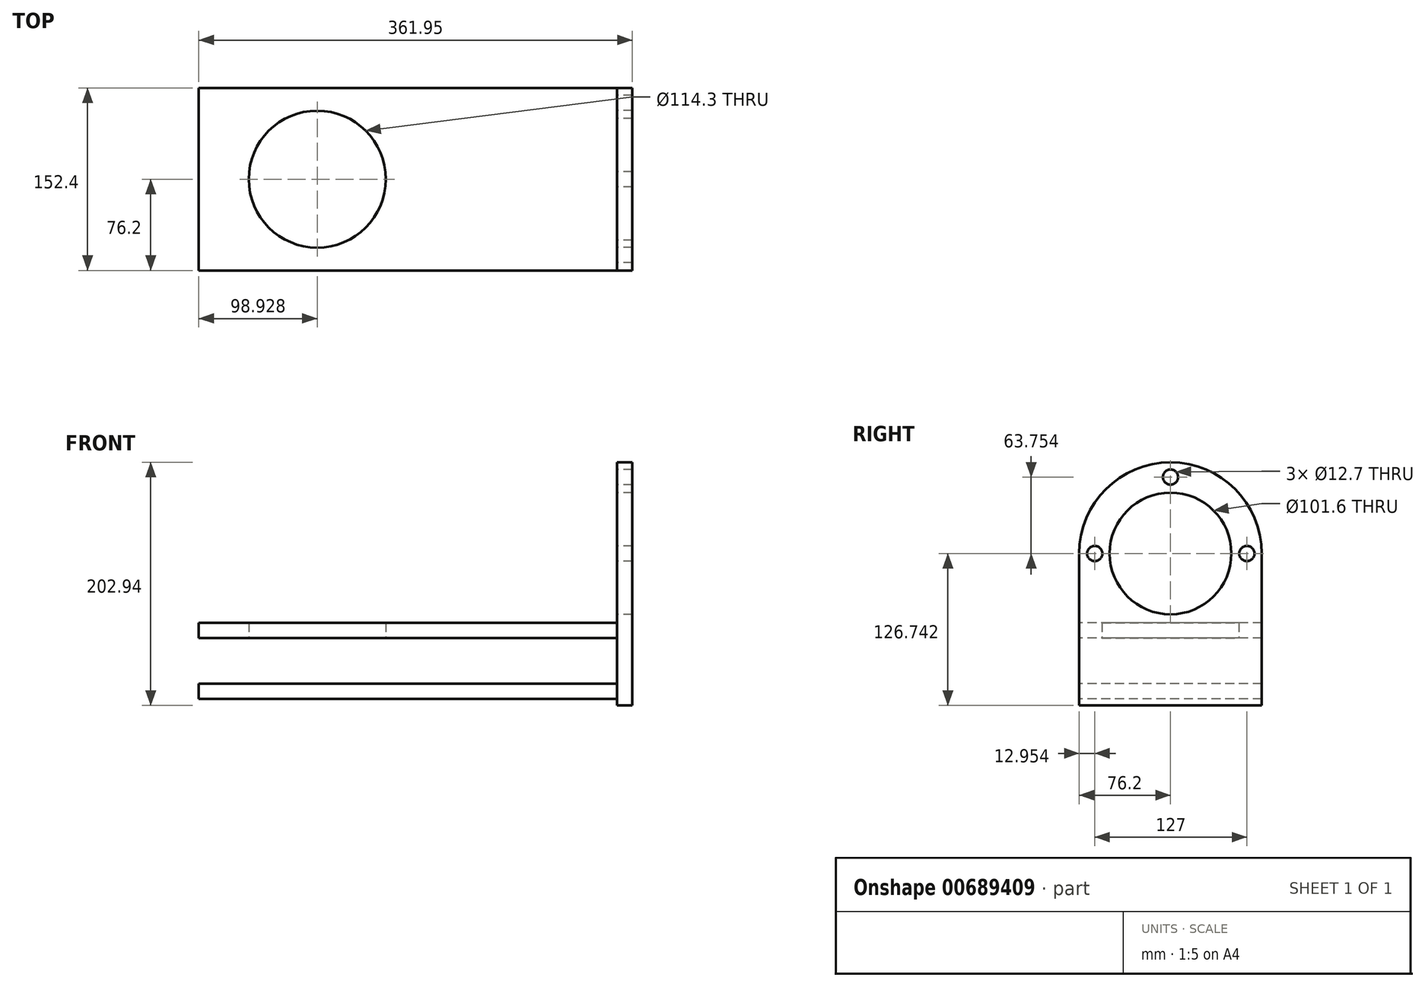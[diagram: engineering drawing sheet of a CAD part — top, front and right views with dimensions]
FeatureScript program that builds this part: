
annotation { "Feature Type Name" : "Feature", "Feature Type Description" : "" }
export const myFeature = defineFeature(function(context is Context, id is Id, definition is map)
    precondition{}
    {
        {
            var Q0;
            Q0=qCreatedBy(makeId("Top.planeOp"),FACE);
            var sketch = newSketch(context, id + "F0", { "sketchPlane" : qUnion([Q0])});
            skLineSegment(sketch, "E0.bottom", {"start": v(-174.63, 76.2) * mm, "end": v(174.63, 76.2) * mm});
            skLineSegment(sketch, "E0.top", {"start": v(-174.63, -76.2) * mm, "end": v(174.63, -76.2) * mm});
            skLineSegment(sketch, "E0.left", {"start": v(-174.62, 76.2) * mm, "end": v(-174.63, -76.2) * mm});
            skLineSegment(sketch, "E0.right", {"start": v(174.63, 76.2) * mm, "end": v(174.63, -76.2) * mm});
            skPoint(sketch, "E0.middle", {"position": v(0, 0) * mm});
            skCircle(sketch, "E1", {"center": v(-75.7, 0) * mm, "radius": 57.15 * mm});
            skSolve(sketch);
        }
        {
            var Q0;
            Q0=makeQuery(id+"F0.imprint","IMPRINT",FACE,{"disambiguationData":[TD([[makeQuery(id+"F0.imprint","IMPRINT",EDGE,{"derivedFrom":sQuery(id+"F0.wireOp",EDGE,"E0.bottom")}),-1.0]])]});
            extrude(context, id + "F1", {"entities" : qUnion([Q0]), "depth" : 12.7 * mm, "offsetDistance" : 25.4 * mm});
        }
        {
            var Q0;
            Q0=makeQuery(id+"F1.opExtrude","CAP_FACE",FACE,{"disambiguationData":[OSD([sQuery(id+"F0.wireOp",EDGE,"E0.bottom"),sQuery(id+"F0.wireOp",EDGE,"E0.top"),sQuery(id+"F0.wireOp",EDGE,"E0.left"),sQuery(id+"F0.wireOp",EDGE,"E0.right"),sQuery(id+"F0.wireOp",EDGE,"E1")])],"isStart":false});
            var sketch = newSketch(context, id + "F2", { "sketchPlane" : qUnion([Q0])});
            skLineSegment(sketch, "E2.bottom", {"start": v(-174.63, 76.2) * mm, "end": v(174.63, 76.2) * mm});
            skLineSegment(sketch, "E2.top", {"start": v(-174.63, -76.2) * mm, "end": v(174.62, -76.2) * mm});
            skLineSegment(sketch, "E2.left", {"start": v(-174.63, 76.2) * mm, "end": v(-174.63, -76.2) * mm});
            skLineSegment(sketch, "E2.right", {"start": v(174.63, 76.2) * mm, "end": v(174.62, -76.2) * mm});
            skPoint(sketch, "E2.middle", {"position": v(0, 0) * mm});
            skSolve(sketch);
        }
        {
            var Q0;
            Q0=makeQuery(id+"F2.imprint","IMPRINT",FACE,{"disambiguationData":[TD([[makeQuery(id+"F2.imprint","IMPRINT",EDGE,{"derivedFrom":sQuery(id+"F2.wireOp",EDGE,"E2.bottom")}),-1.0]])]});
            var Q1;
            Q1=makeQuery(id+"F2.imprint","IMPRINT",FACE,{"disambiguationData":[TD([[makeQuery(id+"F2.imprint","IMPRINT",EDGE,{"derivedFrom":makeQuery(id+"F1.opExtrude","CAP_EDGE",EDGE,{"disambiguationData":[OSD([sQuery(id+"F0.wireOp",EDGE,"E1")])],"isStart":false})}),1.0]])]});
            extrude(context, id + "F3", {"entities" : qUnion([Q0, Q1]), "depth" : 12.7 * mm, "offsetDistance" : 25.4 * mm});
        }
        {
            var Q0;
            Q0=makeQuery(id+"F3.opExtrude","SWEPT_BODY",BODY,{"disambiguationData":[OSD([sQuery(id+"F2.wireOp",EDGE,"E2.bottom"),sQuery(id+"F2.wireOp",EDGE,"E2.top"),sQuery(id+"F2.wireOp",EDGE,"E2.left"),sQuery(id+"F2.wireOp",EDGE,"E2.right")])]});
            var Q1;
            Q1=makeQuery(id+"F3.opExtrude","CAP_FACE",FACE,{"disambiguationData":[OSD([sQuery(id+"F2.wireOp",EDGE,"E2.bottom"),sQuery(id+"F2.wireOp",EDGE,"E2.top"),sQuery(id+"F2.wireOp",EDGE,"E2.left"),sQuery(id+"F2.wireOp",EDGE,"E2.right")])],"isStart":false});
            transform(context, id + "F4", {"entities" : qUnion([Q0]), "transformType" : TransformType.TRANSLATION_DISTANCE, "transformDirection" : qUnion([Q1]), "distance" : 63.5 * mm, "oppositeDirection" : true, "makeCopy" : false});
        }
        {
            var Q0;
            Q0=qCreatedBy(makeId("Right.planeOp"),FACE);
            var sketch = newSketch(context, id + "F5", { "sketchPlane" : qUnion([Q0])});
            skLineSegment(sketch, "E3.top", {"start": v(-76.2, -56.13) * mm, "end": v(76.2, -56.13) * mm});
            skPoint(sketch, "E3.middle", {"position": v(0, 0) * mm});
            skLineSegment(sketch, "E4", {"start": v(-76.2, 70.61) * mm, "end": v(-76.2, -56.13) * mm});
            skLineSegment(sketch, "E5", {"start": v(76.2, 70.61) * mm, "end": v(76.2, -56.13) * mm});
            skArc(sketch, "E6", {"start": v(76.2, 70.61) * mm, "mid": v(0, 146.81) * mm, "end": v(-76.2, 70.61) * mm});
            skCircle(sketch, "E7", {"center": v(0, 70.61) * mm, "radius": 50.8 * mm});
            skCircle(sketch, "E8", {"center": v(0, 134.37) * mm, "radius": 6.35 * mm});
            skCircle(sketch, "E9", {"center": v(63.75, 70.61) * mm, "radius": 6.35 * mm});
            skCircle(sketch, "E10", {"center": v(-63.25, 70.61) * mm, "radius": 6.35 * mm});
            skSolve(sketch);
        }
        {
            var Q0;
            Q0=makeQuery(id+"F5.imprint","IMPRINT",FACE,{"disambiguationData":[TD([[makeQuery(id+"F5.imprint","IMPRINT",EDGE,{"derivedFrom":sQuery(id+"F5.wireOp",EDGE,"E3.top")}),1.0]])]});
            extrude(context, id + "F6", {"entities" : qUnion([Q0]), "depth" : 12.7 * mm, "offsetDistance" : 25.4 * mm});
        }
        {
            var Q0;
            Q0=makeQuery(id+"F6.opExtrude","SWEPT_BODY",BODY,{"disambiguationData":[OSD([sQuery(id+"F5.wireOp",EDGE,"E3.top"),sQuery(id+"F5.wireOp",EDGE,"E4"),sQuery(id+"F5.wireOp",EDGE,"E5"),sQuery(id+"F5.wireOp",EDGE,"E6"),sQuery(id+"F5.wireOp",EDGE,"E7"),sQuery(id+"F5.wireOp",EDGE,"E8"),sQuery(id+"F5.wireOp",EDGE,"E9"),sQuery(id+"F5.wireOp",EDGE,"E10")])]});
            var Q1;
            Q1=qCreatedBy(makeId("Right.planeOp"),FACE);
            transform(context, id + "F7", {"entities" : qUnion([Q0]), "transformType" : TransformType.TRANSLATION_DISTANCE, "transformDirection" : qUnion([Q1]), "distance" : 174.62 * mm, "makeCopy" : false});
        }
    });
